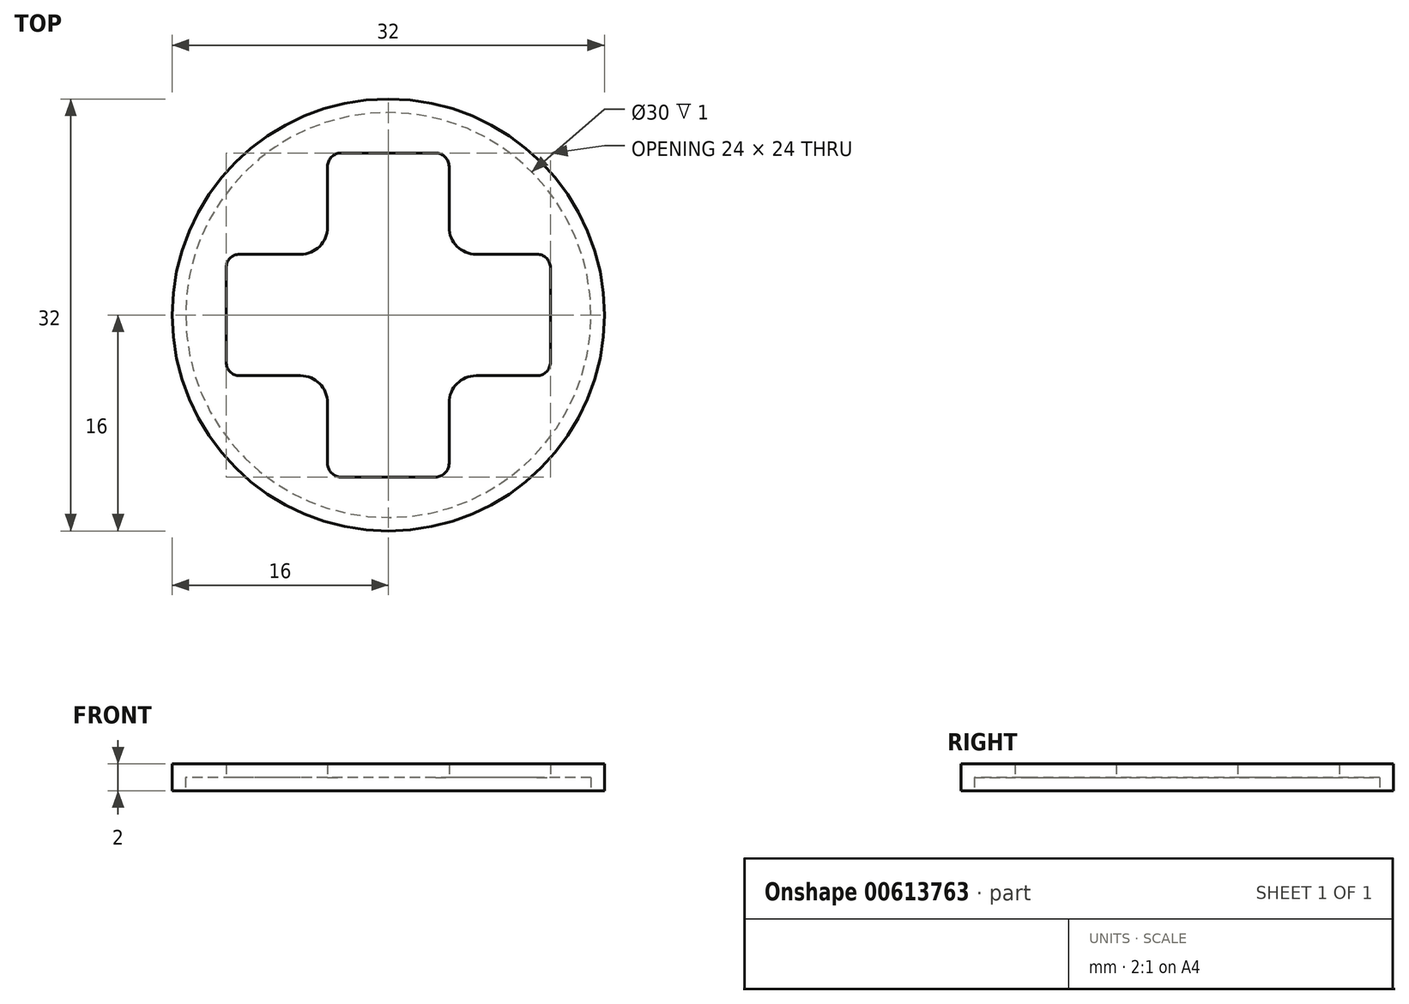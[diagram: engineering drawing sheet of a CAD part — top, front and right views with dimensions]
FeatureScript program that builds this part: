
annotation { "Feature Type Name" : "Feature", "Feature Type Description" : "" }
export const myFeature = defineFeature(function(context is Context, id is Id, definition is map)
    precondition{}
    {
        {
            var Q0;
            Q0=qCreatedBy(makeId("Top.planeOp"),FACE);
            var sketch = newSketch(context, id + "F0", { "sketchPlane" : qUnion([Q0])});
            skLineSegment(sketch, "E0.bottom", {"start": v(4.5, -12) * mm, "end": v(-4.5, -12) * mm});
            skLineSegment(sketch, "E0.top", {"start": v(4.5, 12) * mm, "end": v(-4.5, 12) * mm});
            skLineSegment(sketch, "E0.left", {"start": v(4.5, -12) * mm, "end": v(4.5, 12) * mm});
            skLineSegment(sketch, "E0.right", {"start": v(-4.5, -12) * mm, "end": v(-4.5, 12) * mm});
            skPoint(sketch, "E0.middle", {"position": v(0, 0) * mm});
            skLineSegment(sketch, "E1.bottom", {"start": v(12, -4.5) * mm, "end": v(-12, -4.5) * mm});
            skLineSegment(sketch, "E1.top", {"start": v(12, 4.5) * mm, "end": v(-12, 4.5) * mm});
            skLineSegment(sketch, "E1.left", {"start": v(12, -4.5) * mm, "end": v(12, 4.5) * mm});
            skLineSegment(sketch, "E1.right", {"start": v(-12, -4.5) * mm, "end": v(-12, 4.5) * mm});
            skCircle(sketch, "E2", {"center": v(0, 0) * mm, "radius": 15 * mm});
            skCircle(sketch, "E3", {"center": v(0, 0) * mm, "radius": 16 * mm});
            skSolve(sketch);
        }
        {
            var Q0;
            {var subQ10=sQuery(id+"F0.wireOp",EDGE,"E0.bottom");Q0=makeQuery(id+"F0.imprint","IMPRINT",FACE,{"disambiguationData":[TD([[makeQuery(id+"F0.imprint","IMPRINT",EDGE,{"derivedFrom":subQ10}),1.0]])]});}
            var Q1;
            Q1=makeQuery(id+"F0.imprint","IMPRINT",FACE,{"disambiguationData":[TD([[makeQuery(id+"F0.imprint","IMPRINT",EDGE,{"derivedFrom":sQuery(id+"F0.wireOp",EDGE,"E2")}),-1.0]])]});
            extrude(context, id + "F1", {"entities" : qUnion([Q0, Q1]), "depth" : 2 * mm, "offsetDistance" : 25 * mm});
        }
        {
            var Q0;
            {var subQ10=sQuery(id+"F0.wireOp",EDGE,"E0.bottom");Q0=makeQuery(id+"F0.imprint","IMPRINT",FACE,{"disambiguationData":[TD([[makeQuery(id+"F0.imprint","IMPRINT",EDGE,{"derivedFrom":subQ10}),1.0]])]});}
            extrude(context, id + "F2", {"entities" : qUnion([Q0]), "operationType" : NewBodyOperationType.REMOVE, "oppositeDirection" : true, "depth" : -1 * mm, "offsetDistance" : 25 * mm});
        }
        {
            var Q0;
            Q0=makeQuery(id+"F1.opExtrude","SWEPT_EDGE",EDGE,{"disambiguationData":[OSD([sQuery(id+"F0.wireOp",EDGE,"E0.top"),sQuery(id+"F0.wireOp",EDGE,"E0.right")])]});
            var Q1;
            Q1=makeQuery(id+"F1.opExtrude","SWEPT_EDGE",EDGE,{"disambiguationData":[OSD([sQuery(id+"F0.wireOp",EDGE,"E0.top"),sQuery(id+"F0.wireOp",EDGE,"E0.left")])]});
            var Q2;
            Q2=makeQuery(id+"F1.opExtrude","SWEPT_EDGE",EDGE,{"disambiguationData":[OSD([sQuery(id+"F0.wireOp",EDGE,"E1.top"),sQuery(id+"F0.wireOp",EDGE,"E1.left")])]});
            var Q3;
            Q3=makeQuery(id+"F1.opExtrude","SWEPT_EDGE",EDGE,{"disambiguationData":[OSD([sQuery(id+"F0.wireOp",EDGE,"E1.bottom"),sQuery(id+"F0.wireOp",EDGE,"E1.left")])]});
            var Q4;
            Q4=makeQuery(id+"F1.opExtrude","SWEPT_EDGE",EDGE,{"disambiguationData":[OSD([sQuery(id+"F0.wireOp",EDGE,"E0.bottom"),sQuery(id+"F0.wireOp",EDGE,"E0.left")])]});
            var Q5;
            Q5=makeQuery(id+"F1.opExtrude","SWEPT_EDGE",EDGE,{"disambiguationData":[OSD([sQuery(id+"F0.wireOp",EDGE,"E0.bottom"),sQuery(id+"F0.wireOp",EDGE,"E0.right")])]});
            var Q6;
            Q6=makeQuery(id+"F1.opExtrude","SWEPT_EDGE",EDGE,{"disambiguationData":[OSD([sQuery(id+"F0.wireOp",EDGE,"E1.bottom"),sQuery(id+"F0.wireOp",EDGE,"E1.right")])]});
            var Q7;
            Q7=makeQuery(id+"F1.opExtrude","SWEPT_EDGE",EDGE,{"disambiguationData":[OSD([sQuery(id+"F0.wireOp",EDGE,"E1.top"),sQuery(id+"F0.wireOp",EDGE,"E1.right")])]});
            fillet(context, id + "F3", {"entities" : qUnion([Q0, Q1, Q2, Q3, Q4, Q5, Q6, Q7]), "radius" : 1 * mm, "tangentPropagation" : true, "allowEdgeOverflow" : false});
        }
        {
            var Q0;
            Q0=makeQuery(id+"F1.opExtrude","SWEPT_EDGE",EDGE,{"disambiguationData":[OSD([sQuery(id+"F0.wireOp",EDGE,"E0.right"),sQuery(id+"F0.wireOp",EDGE,"E1.top")])]});
            var Q1;
            Q1=makeQuery(id+"F1.opExtrude","SWEPT_EDGE",EDGE,{"disambiguationData":[OSD([sQuery(id+"F0.wireOp",EDGE,"E0.left"),sQuery(id+"F0.wireOp",EDGE,"E1.top")])]});
            var Q2;
            Q2=makeQuery(id+"F1.opExtrude","SWEPT_EDGE",EDGE,{"disambiguationData":[OSD([sQuery(id+"F0.wireOp",EDGE,"E0.left"),sQuery(id+"F0.wireOp",EDGE,"E1.bottom")])]});
            var Q3;
            Q3=makeQuery(id+"F1.opExtrude","SWEPT_EDGE",EDGE,{"disambiguationData":[OSD([sQuery(id+"F0.wireOp",EDGE,"E0.right"),sQuery(id+"F0.wireOp",EDGE,"E1.bottom")])]});
            fillet(context, id + "F4", {"entities" : qUnion([Q0, Q1, Q2, Q3]), "radius" : 2 * mm, "tangentPropagation" : true, "allowEdgeOverflow" : false});
        }
    });
